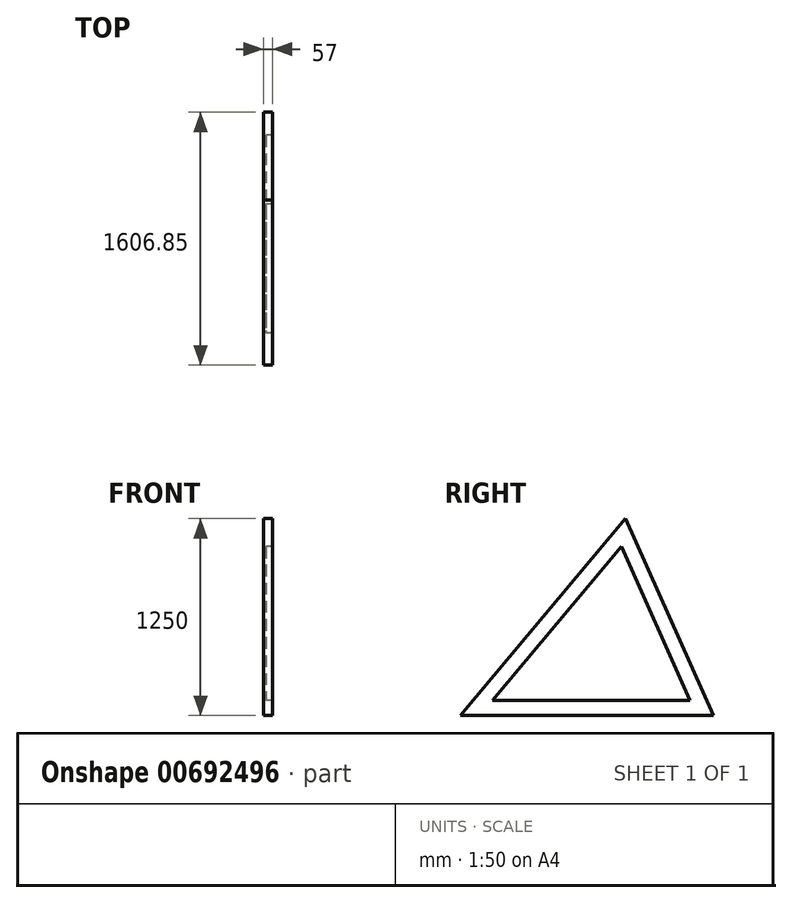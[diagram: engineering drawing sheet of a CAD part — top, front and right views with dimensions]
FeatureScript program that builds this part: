
annotation { "Feature Type Name" : "Feature", "Feature Type Description" : "" }
export const myFeature = defineFeature(function(context is Context, id is Id, definition is map)
    precondition{}
    {
        {
            var Q0;
            Q0=qCreatedBy(makeId("Right.planeOp"),FACE);
            var sketch = newSketch(context, id + "F0", { "sketchPlane" : qUnion([Q0])});
            skPoint(sketch, "E0.MirrorP", {"position": v(89.48, 669.53) * mm});
            skPoint(sketch, "E1.MirrorP", {"position": v(-810.44, -403.07) * mm});
            skPoint(sketch, "E2.MirrorP", {"position": v(-730.73, -308.07) * mm});
            skPoint(sketch, "E3.MirrorP", {"position": v(568.38, -403.07) * mm});
            skLineSegment(sketch, "E4.MirrorCS", {"start": v(525.96, -308.07) * mm, "end": v(-730.73, -308.07) * mm});
            skLineSegment(sketch, "E5.MirrorCS", {"start": v(89.48, 669.53) * mm, "end": v(-810.44, -403.07) * mm});
            skPoint(sketch, "E6.MirrorP", {"position": v(114.3, 846.93) * mm});
            skLineSegment(sketch, "E7.MirrorCS", {"start": v(525.96, -308.07) * mm, "end": v(568.38, -403.07) * mm});
            skLineSegment(sketch, "E8.MirrorCS", {"start": v(672.41, -403.07) * mm, "end": v(-934.44, -403.07) * mm});
            skLineSegment(sketch, "E9.MirrorCS", {"start": v(-934.44, -403.07) * mm, "end": v(114.3, 846.93) * mm});
            skPoint(sketch, "E10.MirrorP", {"position": v(672.41, -403.07) * mm});
            skLineSegment(sketch, "E11.MirrorCS", {"start": v(672.41, -403.07) * mm, "end": v(114.3, 846.93) * mm});
            skLineSegment(sketch, "E12.MirrorCS", {"start": v(525.96, -308.07) * mm, "end": v(46.4, 766) * mm});
            skPoint(sketch, "E13.MirrorP", {"position": v(525.96, -308.07) * mm});
            skPoint(sketch, "E14.MirrorP", {"position": v(46.4, 766) * mm});
            skSolve(sketch);
        }
        {
            var Q0;
            {var subQ2=sQuery(id+"F0.wireOp",EDGE,"E8.MirrorCS");var subQ4=sQuery(id+"F0.wireOp",EDGE,"E9.MirrorCS");var subQ5=makeQuery(id+"F0.imprint","INTERSECT",VERTEX,{"derivedFrom":[subQ2,subQ4]});Q0=makeQuery(id+"F0.imprint","IMPRINT",FACE,{"disambiguationData":[TD([[makeQuery(id+"F0.imprint","IMPRINT",EDGE,{"disambiguationData":[TD([[subQ5,1.0]])],"derivedFrom":subQ2}),-1.0]])]});}
            var Q1;
            {var subQ2=sQuery(id+"F0.wireOp",EDGE,"E7.MirrorCS");Q1=makeQuery(id+"F0.imprint","IMPRINT",FACE,{"disambiguationData":[TD([[makeQuery(id+"F0.imprint","IMPRINT",EDGE,{"derivedFrom":subQ2}),1.0]])]});}
            var Q2;
            {var subQ0=sQuery(id+"F0.wireOp",EDGE,"E7.MirrorCS");Q2=makeQuery(id+"F0.imprint","IMPRINT",FACE,{"disambiguationData":[TD([[makeQuery(id+"F0.imprint","IMPRINT",EDGE,{"derivedFrom":subQ0}),-1.0]])]});}
            extrude(context, id + "F1", {"entities" : qUnion([Q0, Q1, Q2]), "depth" : 57 * mm, "offsetDistance" : 25.4 * mm});
        }
        {
            var Q0;
            {var subQ0=sQuery(id+"F0.wireOp",EDGE,"E4.MirrorCS");Q0=makeQuery(id+"F0.imprint","IMPRINT",FACE,{"disambiguationData":[TD([[makeQuery(id+"F0.imprint","IMPRINT",EDGE,{"derivedFrom":subQ0}),-1.0]])]});}
            extrude(context, id + "F2", {"entities" : qUnion([Q0]), "operationType" : NewBodyOperationType.ADD, "depth" : 18 * mm, "offsetDistance" : 25.4 * mm});
        }
    });
